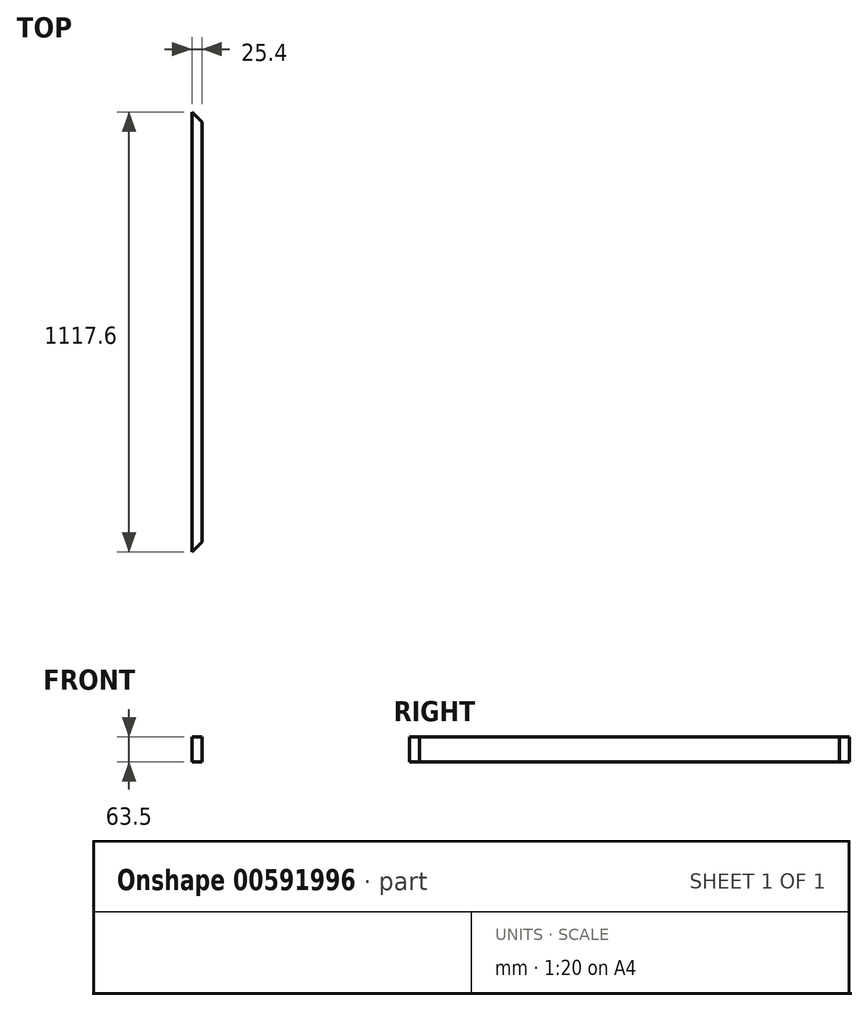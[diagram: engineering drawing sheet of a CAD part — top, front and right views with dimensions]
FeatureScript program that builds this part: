
annotation { "Feature Type Name" : "Feature", "Feature Type Description" : "" }
export const myFeature = defineFeature(function(context is Context, id is Id, definition is map)
    precondition{}
    {
        {
            var Q0;
            Q0=qCreatedBy(makeId("Top.planeOp"),FACE);
            var sketch = newSketch(context, id + "F0", { "sketchPlane" : qUnion([Q0])});
            skLineSegment(sketch, "E0", {"start": v(-11.08, 570.82) * mm, "end": v(-11.08, -546.78) * mm});
            skLineSegment(sketch, "E1", {"start": v(-11.08, 570.82) * mm, "end": v(14.32, 545.42) * mm});
            skPoint(sketch, "E2.endSnap0", {"position": v(-11.08, 12.02) * mm});
            skLineSegment(sketch, "E3.MirrorCS", {"start": v(-11.08, -546.78) * mm, "end": v(14.32, -521.38) * mm});
            skLineSegment(sketch, "E4", {"start": v(14.32, 545.42) * mm, "end": v(14.32, -521.38) * mm});
            skSolve(sketch);
        }
        {
            var Q0;
            Q0 = qSketchRegion(id + "F0", true);
            extrude(context, id + "F1", {"entities" : qUnion([Q0]), "depth" : 63.5 * mm, "offsetDistance" : 25.4 * mm});
        }
    });
